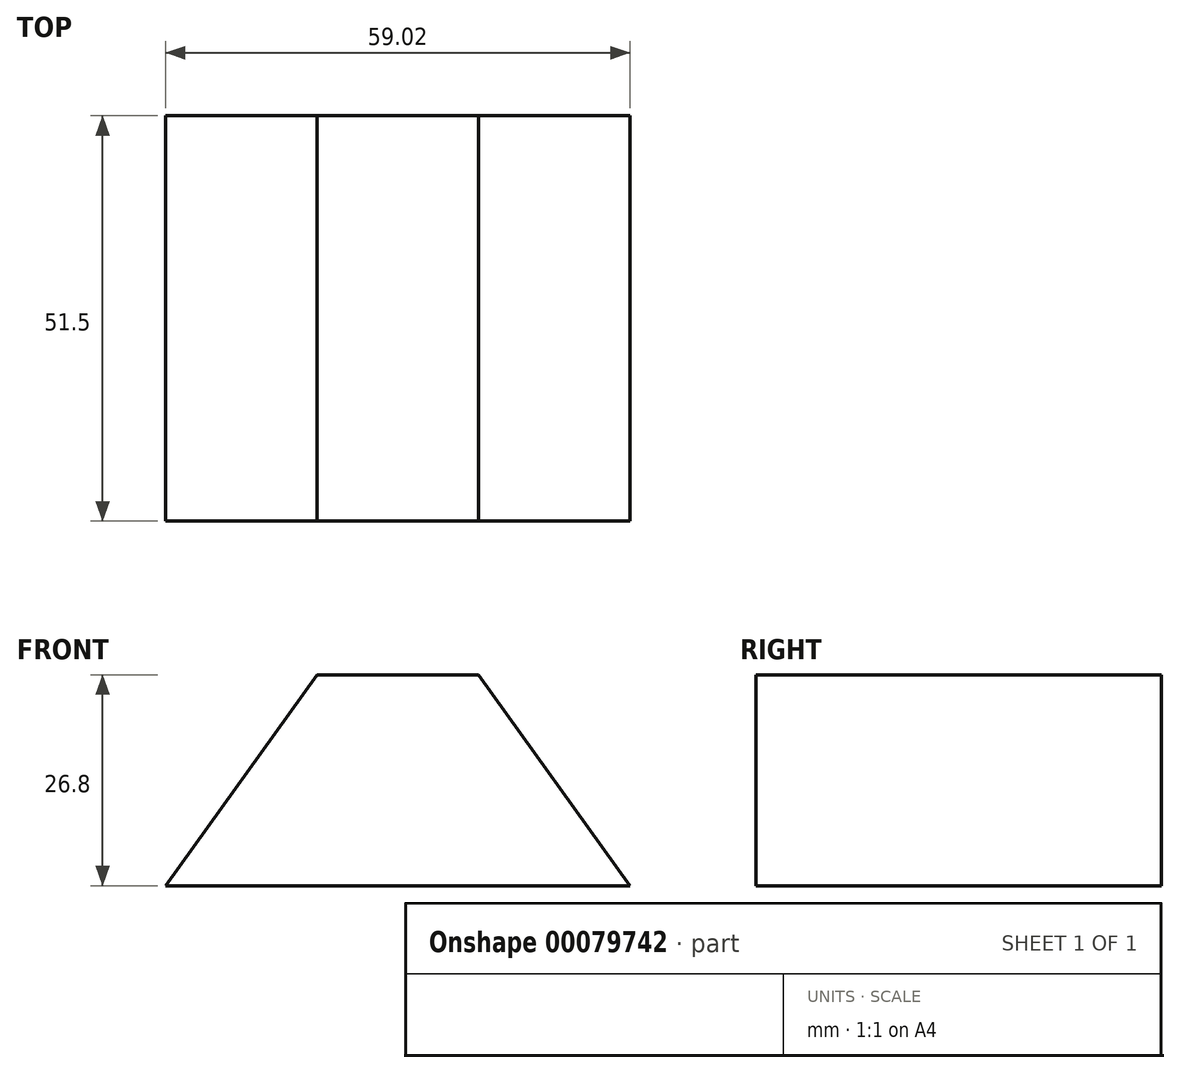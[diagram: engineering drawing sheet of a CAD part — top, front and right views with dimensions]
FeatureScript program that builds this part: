
annotation { "Feature Type Name" : "Feature", "Feature Type Description" : "" }
export const myFeature = defineFeature(function(context is Context, id is Id, definition is map)
    precondition{}
    {
        {
            var Q0;
            Q0=qCreatedBy(makeId("Front.planeOp"),FACE);
            var sketch = newSketch(context, id + "F0", { "sketchPlane" : qUnion([Q0])});
            skLineSegment(sketch, "E0", {"start": v(-29.5, 0) * mm, "end": v(29.5, 0) * mm});
            skLineSegment(sketch, "E1", {"start": v(29.5, 0) * mm, "end": v(10.25, 26.8) * mm});
            skLineSegment(sketch, "E2", {"start": v(10.25, 26.8) * mm, "end": v(-10.25, 26.8) * mm});
            skLineSegment(sketch, "E3", {"start": v(-10.25, 26.8) * mm, "end": v(-29.5, 0) * mm});
            skLineSegment(sketch, "E4.bottom", {"start": v(-5, 0) * mm, "end": v(5, 0) * mm});
            skLineSegment(sketch, "E4.top", {"start": v(-5, 8.67) * mm, "end": v(5, 8.67) * mm});
            skLineSegment(sketch, "E4.left", {"start": v(-5, 0) * mm, "end": v(-5, 8.67) * mm});
            skLineSegment(sketch, "E4.right", {"start": v(5, 0) * mm, "end": v(5, 8.67) * mm});
            skSolve(sketch);
        }
        {
            var Q0;
            Q0 = qSketchRegion(id + "F0", true);
            extrude(context, id + "F1", {"entities" : qUnion([Q0]), "depth" : 51.5 * mm});
        }
    });
